# Revit family: Caroma Teo 600 Wall Basin
name_source: partatom
category: Plumbing Fixtures
revit_build: Autodesk Revit LT 2014 (Build: 20130308_1515(x64)
units: mm (PartAtom-declared; Revit-internal decimal feet)

## types (1)
- Teo 600 - 0 Tap Holes
    1 Taphole = No
    3 Tapholes = No
    Assembly Code = D2010310
    CW Connection = No
    Capacity_ANZRS = 7.0 L
    Default Elevation = 865 mm
    Description = Caroma Teo 600 Wall Basin
    HW Connection = No
    Height_ANZRS = 145 mm  [stored 0.475722 ft]
    Length_ANZRS = 605 mm  [stored 1.98491 ft]
    Manufacturer = GWA Bathrooms & Kitchens
    Material_ANZRS = Porcelain-White-Caroma
    Model = EU8031B05
    ModifiedIssue_ANZRS = 20141103.01 $
    Spout Penetration = 100 mm  [stored 0.328084 ft]
    Tap Penetrations = 100 mm  [stored 0.328084 ft]
    Type Comments = White Only, Overflow Only, Chrome flush fitting waste and white plug supplied
    URL = http://www.caroma.com.au
    Vent Connection = No
    WFU = 1
    Waste = Metal-Chrome-Caroma
    Waste Connection = Yes
    WasteOutlet_ANZRS = 0
    Width_ANZRS = 460 mm  [stored 1.50919 ft]

note: [stored X ft] marks values corroborated as IEEE doubles in the binary element streams (Revit-internal decimal feet)

## geometry (parser evidence)
native form markers: Blend x10, Sweep x2
no freeform markers — native parametric forms only
